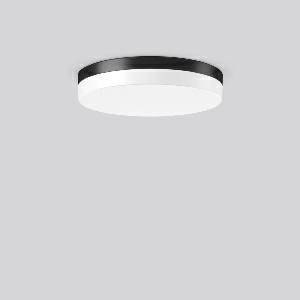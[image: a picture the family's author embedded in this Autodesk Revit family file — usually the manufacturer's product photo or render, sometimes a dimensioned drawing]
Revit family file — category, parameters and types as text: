
# Revit family: flat_slim_round_312632_0031_1_19_dd87
name_source: partatom
category: Lighting Fixtures
units: mm (PartAtom-declared; Revit-internal decimal feet)

## family parameters
Cut with Voids When Loaded = No
Host = Face
Light Source = No
Part Type = Normal
Room Calculation Point = No
Round Connector Dimension = Use Diameter
Shared = No

## types (1)
- MultiLumen 1 830 (1 x LED Modul 830, 2450 lm, 3000)
    Apparent Load = 18 VA
    CIE Flux Codes = 37 67 88 84 100
    Color Rendering = 80
    Color Temperature = 3000
    Default Elevation = 1800 mm
    Height = 70 mm
    Lamp = 1 x LED Modul 830
    Lamp Light Flux = 2450 lm
    Lamp count = 1
    Length = 400 mm
    Lifetime = 50000 h
    Luminous efficacy = 136 lm/W
    Manufacturer = RZB
    ModVariant = No
    Model = 312632.0031.1.19
    Mounting Place = Ceiling
    Mounting Type = Surface mounted
    Number of Poles = 1
    OnlyDefault = Yes
    Power Factor = 1
    Product Name = FLAT SLIM round
    Product group = Surface mounted ceiling and wall luminaires
    ProductGroupID = 305
    Protection Class = Protection class I
    Protection Degree = Degree of protection
    RLX_Detail_Level = 1
    RLX_Emergency_Light_Flux = 0 lm
    RLX_Emergency_Type = 0
    RLX_Emergency_Type_DB = No
    RlxData = <blob elided: 22213 chars, md5=38b07a69>
    Socket = socket
    Standby Power = 0 W
    System Light Flux = 2450 lm
    System Power = 18 W
    Type Comments = MultiLumen 1 830
    Type Image = 312631.0031.jpg
    URL = http://relux.com
    VarID = multilumen_1_830
    Voltage = 0 V
    Weight = 0.00 kg
    Width = 0 mm  [stored 0 ft]

note: [stored X ft] marks values corroborated as IEEE doubles in the binary element streams (Revit-internal decimal feet)

## geometry (parser evidence)
native form markers: Blend x4, Sweep x12
no freeform markers — native parametric forms only
